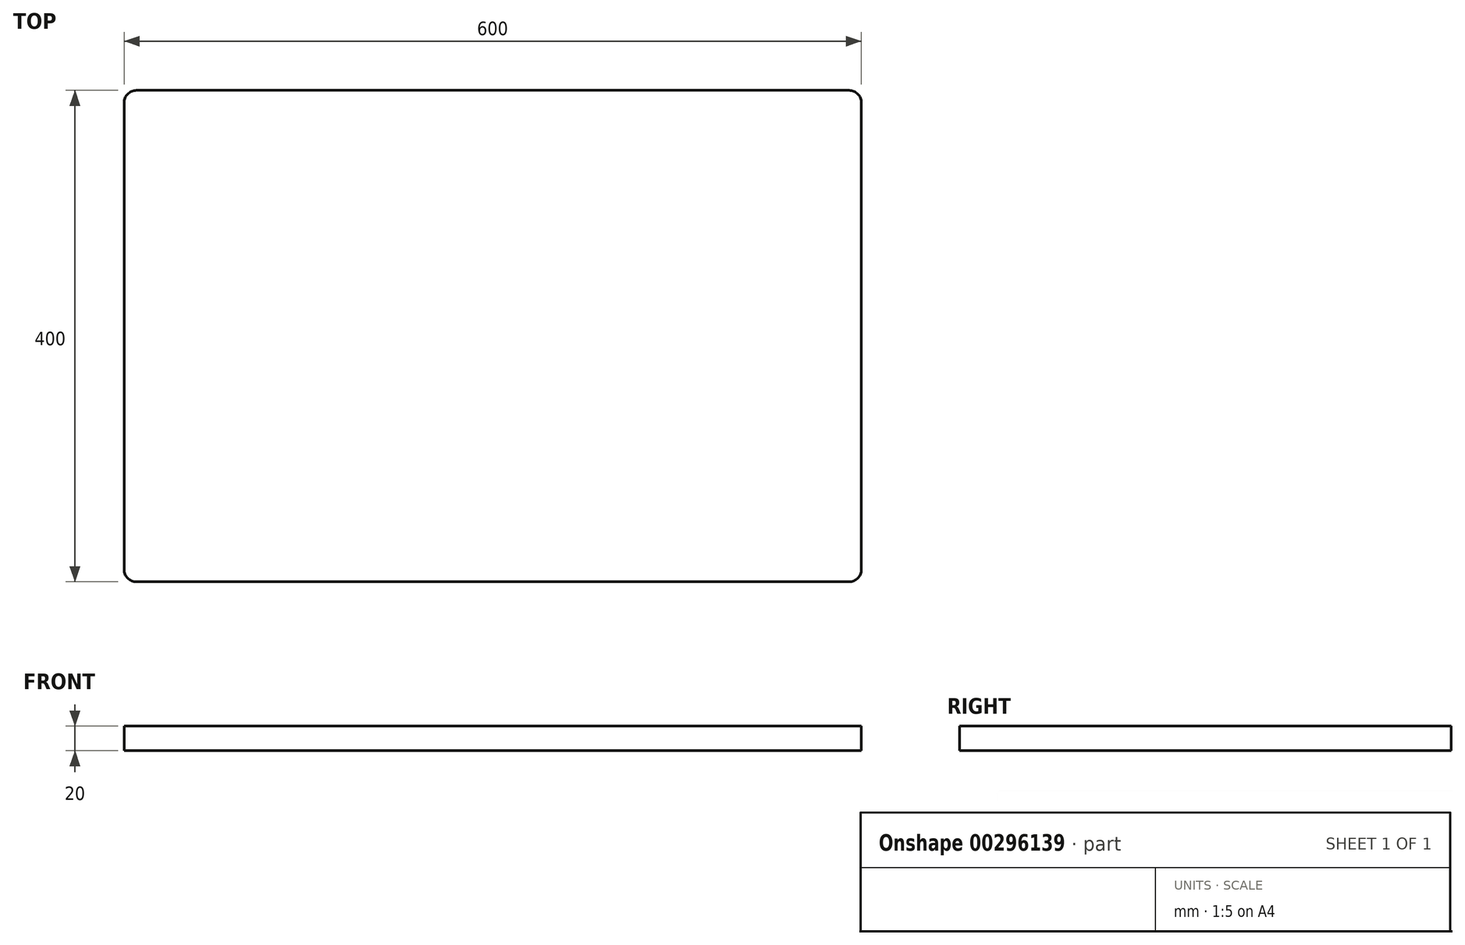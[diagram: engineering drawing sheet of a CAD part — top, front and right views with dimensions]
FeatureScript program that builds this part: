
annotation { "Feature Type Name" : "Feature", "Feature Type Description" : "" }
export const myFeature = defineFeature(function(context is Context, id is Id, definition is map)
    precondition{}
    {
        {
            var Q0;
            Q0=qCreatedBy(makeId("Top.planeOp"),FACE);
            var sketch = newSketch(context, id + "F0", { "sketchPlane" : qUnion([Q0])});
            skLineSegment(sketch, "E0.bottom", {"start": v(-290, 200) * mm, "end": v(290, 200) * mm});
            skLineSegment(sketch, "E0.top", {"start": v(-290, -200) * mm, "end": v(290, -200) * mm});
            skLineSegment(sketch, "E0.left", {"start": v(-300, 190) * mm, "end": v(-300, -190) * mm});
            skLineSegment(sketch, "E0.right", {"start": v(300, 190) * mm, "end": v(300, -190) * mm});
            skPoint(sketch, "E0.middle", {"position": v(0, 0) * mm});
            skPoint(sketch, "E1.visualSharp", {"position": v(-300, -200) * mm});
            skArc(sketch, "E1.filletArc", {"start": v(-300, -190) * mm, "mid": v(-297.07, -197.07) * mm, "end": v(-290, -200) * mm});
            skPoint(sketch, "E2.visualSharp", {"position": v(-300, 200) * mm});
            skArc(sketch, "E2.filletArc", {"start": v(-290, 200) * mm, "mid": v(-297.07, 197.07) * mm, "end": v(-300, 190) * mm});
            skPoint(sketch, "E3.visualSharp", {"position": v(300, 200) * mm});
            skArc(sketch, "E3.filletArc", {"start": v(300, 190) * mm, "mid": v(297.07, 197.07) * mm, "end": v(290, 200) * mm});
            skPoint(sketch, "E4.visualSharp", {"position": v(300, -200) * mm});
            skArc(sketch, "E4.filletArc", {"start": v(290, -200) * mm, "mid": v(297.07, -197.07) * mm, "end": v(300, -190) * mm});
            skSolve(sketch);
        }
        {
            var Q0;
            Q0=qSketchRegion(id+"F0",true);
            extrude(context, id + "F1", {"entities" : qUnion([Q0]), "oppositeDirection" : true, "depth" : 20 * mm});
        }
    });
